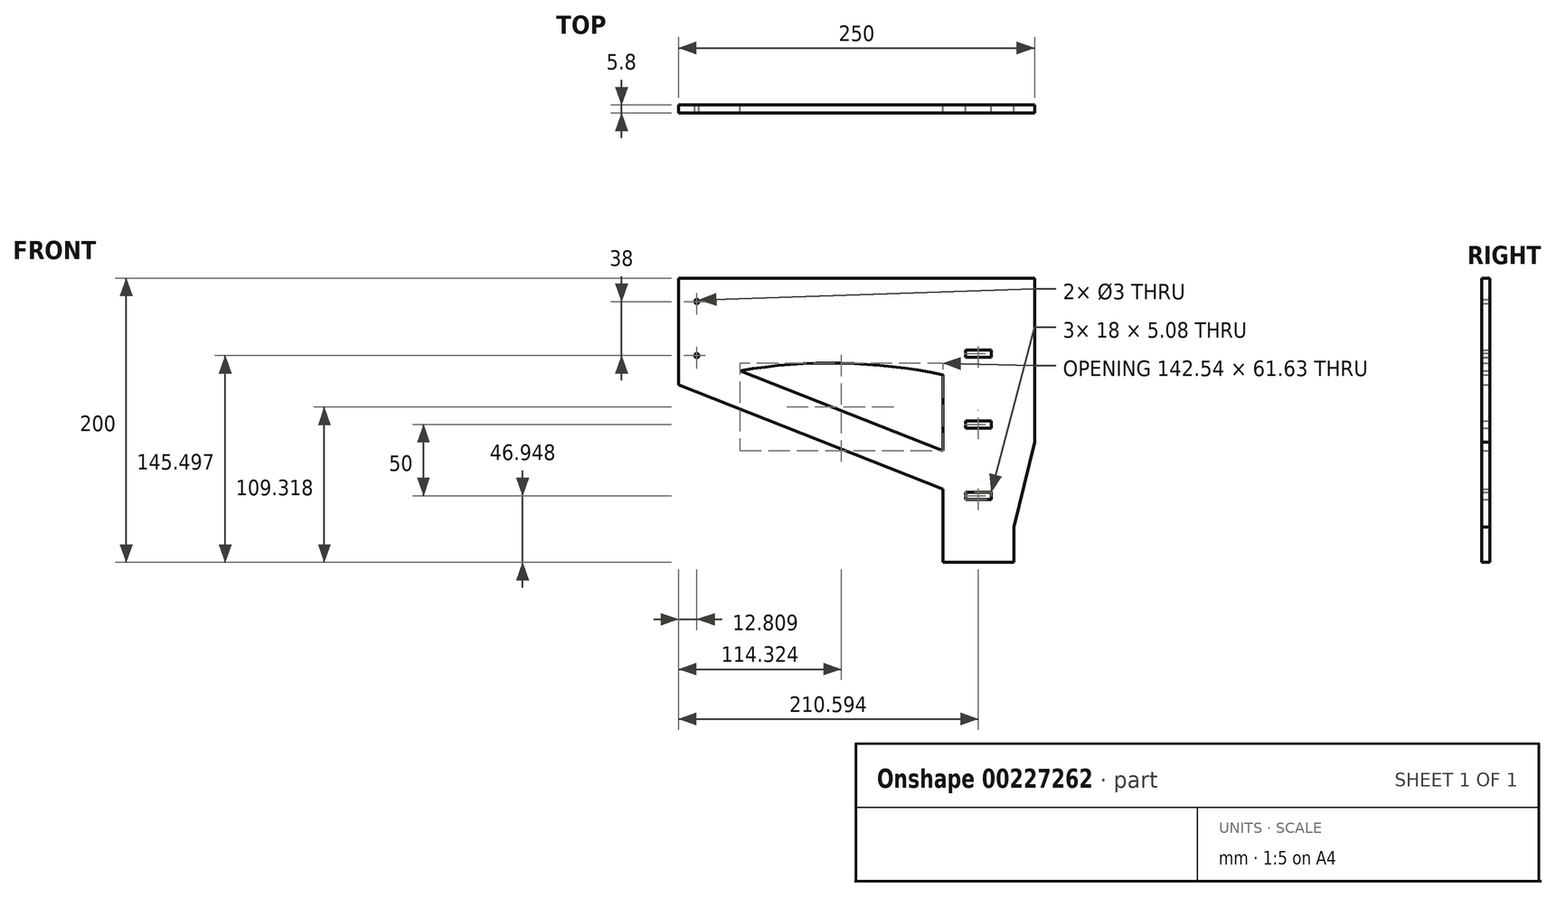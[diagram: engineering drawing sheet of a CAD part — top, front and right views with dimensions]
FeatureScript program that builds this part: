
annotation { "Feature Type Name" : "Feature", "Feature Type Description" : "" }
export const myFeature = defineFeature(function(context is Context, id is Id, definition is map)
    precondition{}
    {
        {
            var Q0;
            Q0=qCreatedBy(makeId("Front.planeOp"),FACE);
            var sketch = newSketch(context, id + "F0", { "sketchPlane" : qUnion([Q0])});
            skLineSegment(sketch, "E0.top", {"start": v(127.28, 55.74) * mm, "end": v(-122.72, 55.74) * mm});
            skLineSegment(sketch, "E0.left", {"start": v(127.28, -59.51) * mm, "end": v(127.28, 55.74) * mm});
            skLineSegment(sketch, "E0.right", {"start": v(-122.72, -19.26) * mm, "end": v(-122.72, 55.74) * mm});
            skArc(sketch, "E1", {"start": v(62.87, -12.25) * mm, "mid": v(-30.35, -4.32) * mm, "end": v(-122.72, -19.26) * mm});
            skPoint(sketch, "E2.orphan", {"position": v(-122.72, -59.51) * mm});
            skLineSegment(sketch, "E3", {"start": v(62.87, -12.25) * mm, "end": v(62.87, -119.26) * mm});
            skLineSegment(sketch, "E4", {"start": v(62.87, -119.26) * mm, "end": v(112.87, -119.26) * mm});
            skLineSegment(sketch, "E5", {"start": v(112.87, -119.26) * mm, "end": v(127.28, -59.51) * mm});
            skLineSegment(sketch, "E6", {"start": v(-122.72, -19.26) * mm, "end": v(62.87, -92.64) * mm});
            skLineSegment(sketch, "E7", {"start": v(62.87, -65.76) * mm, "end": v(-79.67, -9.4) * mm});
            skLineSegment(sketch, "E8.top", {"start": v(-122.72, 0.24) * mm, "end": v(127.28, 0.24) * mm});
            skLineSegment(sketch, "E8.left", {"start": v(-122.72, 45.49) * mm, "end": v(-122.72, 0.24) * mm});
            skLineSegment(sketch, "E9.bottom", {"start": v(-122.72, 45.49) * mm, "end": v(127.28, 45.49) * mm});
            skLineSegment(sketch, "E9.top", {"start": v(-122.72, 10.49) * mm, "end": v(127.28, 10.49) * mm});
            skLineSegment(sketch, "E9.left", {"start": v(-122.72, 45.49) * mm, "end": v(-122.72, 10.49) * mm});
            skLineSegment(sketch, "E9.right", {"start": v(127.28, 45.49) * mm, "end": v(127.28, 10.49) * mm});
            skLineSegment(sketch, "E10.direction1", {"start": v(-81.72, 10.49) * mm, "end": v(-31.72, 10.49) * mm, "construction": true});
            skLineSegment(sketch, "E11", {"start": v(-122.72, 27.99) * mm, "end": v(127.28, 27.99) * mm, "construction": true});
            skLineSegment(sketch, "E12.bottom", {"start": v(96.87, -99.85) * mm, "end": v(78.87, -99.85) * mm});
            skLineSegment(sketch, "E12.top", {"start": v(96.87, -94.77) * mm, "end": v(78.87, -94.77) * mm});
            skLineSegment(sketch, "E12.left", {"start": v(96.87, -99.85) * mm, "end": v(96.87, -94.77) * mm});
            skLineSegment(sketch, "E12.right", {"start": v(78.87, -99.85) * mm, "end": v(78.87, -94.77) * mm});
            skPoint(sketch, "E12.middle", {"position": v(87.87, -97.31) * mm});
            skPoint(sketch, "E12.middle.positionSnap0", {"position": v(87.87, -119.26) * mm});
            skPoint(sketch, "E12.centerSnap0", {"position": v(87.87, -119.26) * mm});
            skLineSegment(sketch, "E13.0.1.0", {"start": v(96.87, -44.77) * mm, "end": v(78.87, -44.77) * mm});
            skPoint(sketch, "E13.0.1.1", {"position": v(87.87, -47.31) * mm});
            skLineSegment(sketch, "E13.0.1.2", {"start": v(78.87, -49.85) * mm, "end": v(78.87, -44.77) * mm});
            skLineSegment(sketch, "E13.0.1.3", {"start": v(96.87, -49.85) * mm, "end": v(96.87, -44.77) * mm});
            skLineSegment(sketch, "E13.0.1.4", {"start": v(96.87, -49.85) * mm, "end": v(78.87, -49.85) * mm});
            skLineSegment(sketch, "E13.0.2.0", {"start": v(96.87, 5.23) * mm, "end": v(78.87, 5.23) * mm});
            skPoint(sketch, "E13.0.2.1", {"position": v(87.87, 2.69) * mm});
            skLineSegment(sketch, "E13.0.2.2", {"start": v(78.87, 0.15) * mm, "end": v(78.87, 5.23) * mm});
            skLineSegment(sketch, "E13.0.2.3", {"start": v(96.87, 0.15) * mm, "end": v(96.87, 5.23) * mm});
            skLineSegment(sketch, "E13.0.2.4", {"start": v(96.87, 0.15) * mm, "end": v(78.87, 0.15) * mm});
            skLineSegment(sketch, "E13.direction1", {"start": v(78.87, -94.77) * mm, "end": v(103.87, -94.77) * mm, "construction": true});
            skLineSegment(sketch, "E13.direction2", {"start": v(78.87, -94.77) * mm, "end": v(78.87, -44.77) * mm, "construction": true});
            skLineSegment(sketch, "E14", {"start": v(-122.72, -19.26) * mm, "end": v(-94.37, -19.26) * mm, "construction": true});
            skCircle(sketch, "E15", {"center": v(-109.91, 1.24) * mm, "radius": 1.5 * mm});
            skCircle(sketch, "E16.0.1.0", {"center": v(-109.91, 39.24) * mm, "radius": 1.5 * mm});
            skLineSegment(sketch, "E16.direction1", {"start": v(-109.91, 1.24) * mm, "end": v(-84.91, 1.24) * mm, "construction": true});
            skLineSegment(sketch, "E16.direction2", {"start": v(-109.91, 1.24) * mm, "end": v(-109.91, 39.24) * mm, "construction": true});
            skSolve(sketch);
        }
        {
            var Q0;
            Q0 = qSketchRegion(id + "F0", true);
            extrude(context, id + "F1", {"entities" : qUnion([Q0]), "depth" : 5.8 * mm});
        }
        {
            var Q0;
            Q0=makeQuery(id+"F1.opExtrude","SWEPT_FACE",FACE,{"disambiguationData":[OSD([sQuery(id+"F0.wireOp",EDGE,"E4")])]});
            extrude(context, id + "F2", {"entities" : qUnion([Q0]), "operationType" : NewBodyOperationType.ADD, "depth" : 25 * mm});
        }
    });
